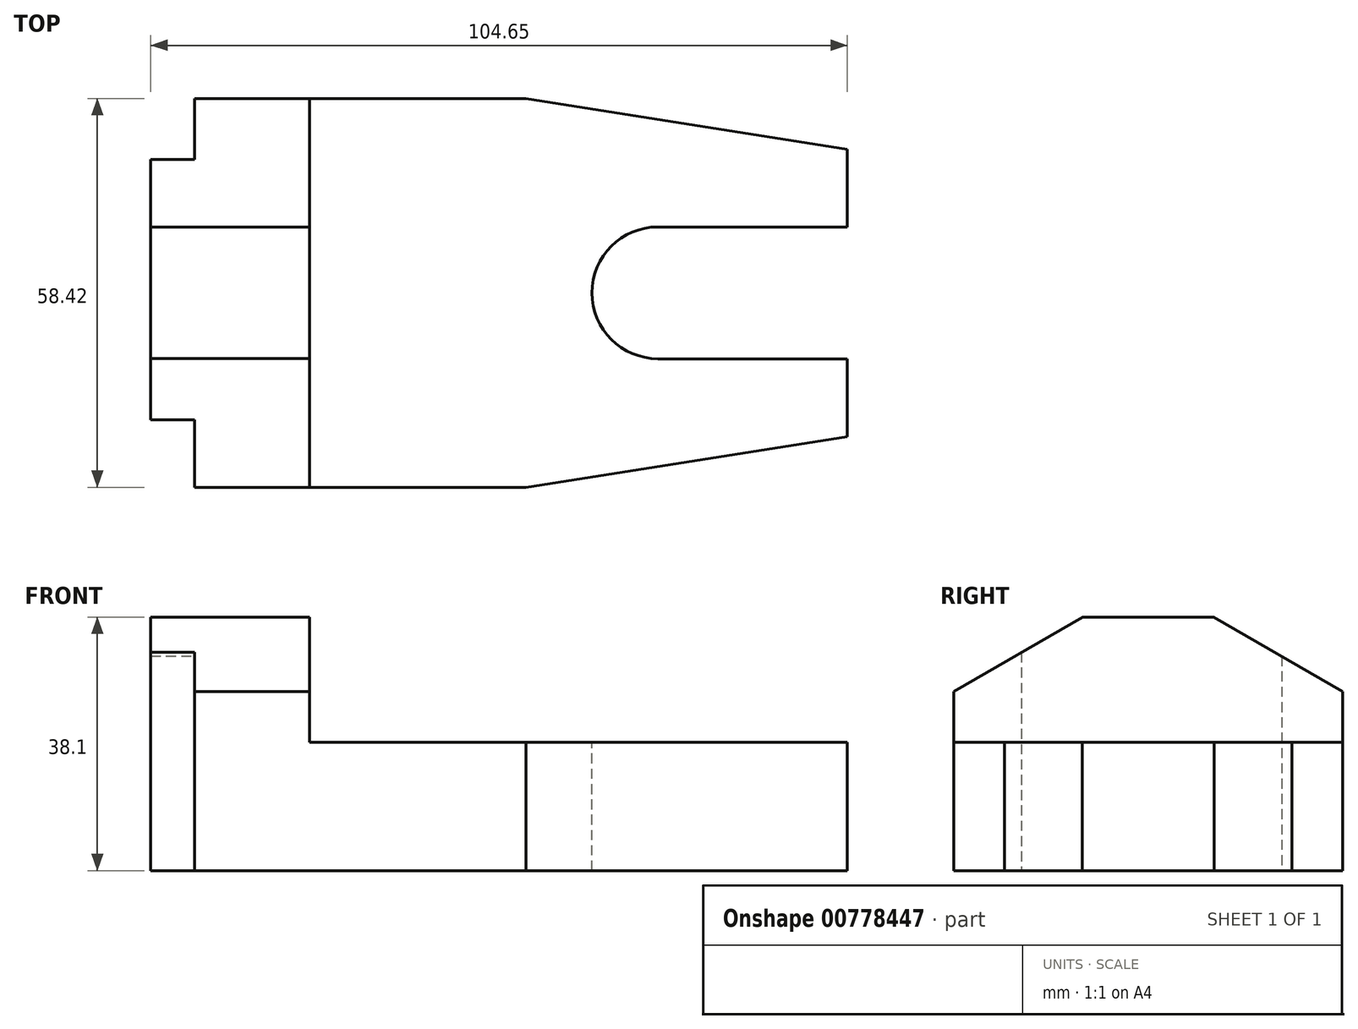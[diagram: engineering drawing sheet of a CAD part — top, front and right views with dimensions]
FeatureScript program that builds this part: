
annotation { "Feature Type Name" : "Feature", "Feature Type Description" : "" }
export const myFeature = defineFeature(function(context is Context, id is Id, definition is map)
    precondition{}
    {
        {
            var Q0;
            Q0=qCreatedBy(makeId("Front.planeOp"),FACE);
            var sketch = newSketch(context, id + "F0", { "sketchPlane" : qUnion([Q0])});
            skLineSegment(sketch, "E0.bottom", {"start": v(0, 0) * mm, "end": v(104.65, 0) * mm});
            skLineSegment(sketch, "E0.top", {"start": v(0, 38.1) * mm, "end": v(104.65, 38.1) * mm});
            skLineSegment(sketch, "E0.left", {"start": v(0, 0) * mm, "end": v(0, 38.1) * mm});
            skLineSegment(sketch, "E0.right", {"start": v(104.65, 0) * mm, "end": v(104.65, 38.1) * mm});
            skSolve(sketch);
        }
        {
            var Q0;
            Q0 = qSketchRegion(id + "F0", true);
            extrude(context, id + "F1", {"entities" : qUnion([Q0]), "depth" : 58.42 * mm, "offsetDistance" : 25.4 * mm});
        }
        {
            var Q0;
            Q0=makeQuery(id+"F1.opExtrude","CAP_FACE",FACE,{"disambiguationData":[OSD([sQuery(id+"F0.wireOp",EDGE,"E0.bottom"),sQuery(id+"F0.wireOp",EDGE,"E0.top"),sQuery(id+"F0.wireOp",EDGE,"E0.left"),sQuery(id+"F0.wireOp",EDGE,"E0.right")])],"isStart":false});
            var sketch = newSketch(context, id + "F2", { "sketchPlane" : qUnion([Q0])});
            skLineSegment(sketch, "E1", {"start": v(0, 38.1) * mm, "end": v(23.88, 38.1) * mm});
            skLineSegment(sketch, "E2", {"start": v(23.88, 38.1) * mm, "end": v(23.88, 19.3) * mm});
            skLineSegment(sketch, "E3", {"start": v(23.88, 19.3) * mm, "end": v(104.65, 19.3) * mm});
            skLineSegment(sketch, "E4", {"start": v(104.65, 19.3) * mm, "end": v(104.65, 0) * mm});
            skSolve(sketch);
        }
        {
            var Q0;
            {var subQ0=sQuery(id+"F2.wireOp",EDGE,"E2");Q0=makeQuery(id+"F2.imprint","IMPRINT",FACE,{"disambiguationData":[TD([[makeQuery(id+"F2.imprint","IMPRINT",EDGE,{"derivedFrom":subQ0}),1.0]])]});}
            extrude(context, id + "F3", {"entities" : qUnion([Q0]), "operationType" : NewBodyOperationType.REMOVE, "oppositeDirection" : true, "depth" : 58.42 * mm, "offsetDistance" : 25.4 * mm});
        }
        {
            var Q0;
            Q0=makeQuery(id+"F3.boolean.opBoolean","COPY",FACE,{"derivedFrom":makeQuery(id+"F3.opExtrude","SWEPT_FACE",FACE,{"disambiguationData":[OSD([sQuery(id+"F2.wireOp",EDGE,"E3")])]})});
            var sketch = newSketch(context, id + "F4", { "sketchPlane" : qUnion([Q0])});
            skLineSegment(sketch, "E5", {"start": v(104.65, -58.42) * mm, "end": v(56.39, -58.42) * mm});
            skLineSegment(sketch, "E6", {"start": v(56.39, -58.42) * mm, "end": v(104.65, -50.8) * mm});
            skLineSegment(sketch, "E7", {"start": v(104.65, -50.8) * mm, "end": v(104.65, -39.12) * mm});
            skLineSegment(sketch, "E8", {"start": v(104.65, -39.12) * mm, "end": v(104.65, -19.3) * mm});
            skLineSegment(sketch, "E9", {"start": v(104.65, -19.3) * mm, "end": v(104.65, -7.62) * mm});
            skLineSegment(sketch, "E10", {"start": v(104.65, -7.62) * mm, "end": v(56.39, 0) * mm});
            skLineSegment(sketch, "E11", {"start": v(56.39, 0) * mm, "end": v(104.65, 0) * mm});
            skLineSegment(sketch, "E12", {"start": v(104.65, 0) * mm, "end": v(104.65, -7.62) * mm});
            skLineSegment(sketch, "E13", {"start": v(104.65, -19.3) * mm, "end": v(76.2, -19.3) * mm});
            skLineSegment(sketch, "E14", {"start": v(104.65, -39.12) * mm, "end": v(76.2, -39.12) * mm});
            skLineSegment(sketch, "E15", {"start": v(76.2, -39.12) * mm, "end": v(76.2, -19.3) * mm});
            skLineSegment(sketch, "E16", {"start": v(76.2, -19.3) * mm, "end": v(76.2, -29.2) * mm});
            skArc(sketch, "E17", {"start": v(76.2, -19.3) * mm, "mid": v(66.3, -29.21) * mm, "end": v(76.2, -39.12) * mm});
            skSolve(sketch);
        }
        {
            var Q0;
            Q0=makeQuery(id+"F4.imprint","IMPRINT",FACE,{"disambiguationData":[TD([[makeQuery(id+"F4.imprint","IMPRINT",EDGE,{"derivedFrom":sQuery(id+"F4.wireOp",EDGE,"E10")}),-1.0]])]});
            var Q1;
            Q1=makeQuery(id+"F4.imprint","IMPRINT",FACE,{"disambiguationData":[TD([[makeQuery(id+"F4.imprint","IMPRINT",EDGE,{"derivedFrom":sQuery(id+"F4.wireOp",EDGE,"E8")}),-1.0]])]});
            var Q2;
            Q2=makeQuery(id+"F4.imprint","IMPRINT",FACE,{"disambiguationData":[TD([[makeQuery(id+"F4.imprint","IMPRINT",EDGE,{"derivedFrom":sQuery(id+"F4.wireOp",EDGE,"E15")}),1.0]])]});
            var Q3;
            {var subQ0=sQuery(id+"F4.wireOp",EDGE,"E5");Q3=makeQuery(id+"F4.imprint","IMPRINT",FACE,{"disambiguationData":[TD([[makeQuery(id+"F4.imprint","IMPRINT",EDGE,{"derivedFrom":subQ0}),1.0]])]});}
            extrude(context, id + "F5", {"entities" : qUnion([Q0, Q1, Q2, Q3]), "operationType" : NewBodyOperationType.REMOVE, "oppositeDirection" : true, "depth" : 19.3 * mm, "offsetDistance" : 25.4 * mm});
        }
        {
            var Q0;
            Q0=makeQuery(id+"F1.opExtrude","SWEPT_FACE",FACE,{"disambiguationData":[OSD([sQuery(id+"F0.wireOp",EDGE,"E0.left")])]});
            var sketch = newSketch(context, id + "F6", { "sketchPlane" : qUnion([Q0])});
            skLineSegment(sketch, "E18", {"start": v(58.42, 38.1) * mm, "end": v(48.26, 38.1) * mm});
            skLineSegment(sketch, "E19", {"start": v(48.26, 38.1) * mm, "end": v(48.26, 0) * mm});
            skLineSegment(sketch, "E20", {"start": v(0, 38.1) * mm, "end": v(10.16, 38.1) * mm});
            skLineSegment(sketch, "E21", {"start": v(9.17, 38.22) * mm, "end": v(9.17, 0) * mm});
            skSolve(sketch);
        }
        {
            var Q0;
            {var subQ1=sQuery(id+"F0.wireOp",EDGE,"E0.left");var subQ2=makeQuery(id+"F1.opExtrude","CAP_EDGE",EDGE,{"disambiguationData":[OSD([subQ1])],"isStart":true});Q0=makeQuery(id+"F6.imprint","IMPRINT",FACE,{"disambiguationData":[TD([[makeQuery(id+"F6.imprint","IMPRINT",EDGE,{"derivedFrom":subQ2}),-1.0]])]});}
            var Q1;
            Q1=makeQuery(id+"F6.imprint","IMPRINT",FACE,{"disambiguationData":[TD([[makeQuery(id+"F6.imprint","IMPRINT",EDGE,{"derivedFrom":sQuery(id+"F6.wireOp",EDGE,"E18")}),1.0]])]});
            extrude(context, id + "F7", {"entities" : qUnion([Q0, Q1]), "operationType" : NewBodyOperationType.REMOVE, "oppositeDirection" : true, "depth" : 6.6 * mm, "offsetDistance" : 25.4 * mm});
        }
        {
            var Q0;
            Q0=makeQuery(id+"F3.boolean.opBoolean","COPY",FACE,{"derivedFrom":makeQuery(id+"F3.opExtrude","SWEPT_FACE",FACE,{"disambiguationData":[OSD([sQuery(id+"F2.wireOp",EDGE,"E2")])]})});
            var sketch = newSketch(context, id + "F8", { "sketchPlane" : qUnion([Q0])});
            skLineSegment(sketch, "E22", {"start": v(0, 19.3) * mm, "end": v(0, 26.92) * mm});
            skLineSegment(sketch, "E23", {"start": v(0, 26.92) * mm, "end": v(-19.36, 38.1) * mm});
            skLineSegment(sketch, "E24", {"start": v(-19.36, 38.1) * mm, "end": v(0, 38.1) * mm});
            skLineSegment(sketch, "E25", {"start": v(0, 38.1) * mm, "end": v(0, 26.92) * mm});
            skSolve(sketch);
        }
        {
            var Q0;
            Q0=makeQuery(id+"F8.imprint","IMPRINT",FACE,{"disambiguationData":[TD([[makeQuery(id+"F8.imprint","IMPRINT",EDGE,{"derivedFrom":sQuery(id+"F8.wireOp",EDGE,"E23")}),-1.0]])]});
            extrude(context, id + "F9", {"entities" : qUnion([Q0]), "operationType" : NewBodyOperationType.REMOVE, "oppositeDirection" : true, "depth" : 23.88 * mm, "offsetDistance" : 25.4 * mm});
        }
        {
            var Q0;
            Q0=makeQuery(id+"F3.boolean.opBoolean","COPY",FACE,{"derivedFrom":makeQuery(id+"F3.opExtrude","SWEPT_FACE",FACE,{"disambiguationData":[OSD([sQuery(id+"F2.wireOp",EDGE,"E2")])]})});
            var sketch = newSketch(context, id + "F10", { "sketchPlane" : qUnion([Q0])});
            skLineSegment(sketch, "E26", {"start": v(-58.42, 19.3) * mm, "end": v(-58.42, 26.92) * mm});
            skLineSegment(sketch, "E27", {"start": v(-58.42, 26.92) * mm, "end": v(-39.06, 38.1) * mm});
            skLineSegment(sketch, "E28", {"start": v(-39.06, 38.1) * mm, "end": v(-58.42, 38.1) * mm});
            skLineSegment(sketch, "E29", {"start": v(-58.42, 38.1) * mm, "end": v(-58.42, 26.92) * mm});
            skSolve(sketch);
        }
        {
            var Q0;
            Q0 = qSketchRegion(id + "F10", true);
            extrude(context, id + "F11", {"entities" : qUnion([Q0]), "operationType" : NewBodyOperationType.REMOVE, "oppositeDirection" : true, "depth" : 23.88 * mm, "offsetDistance" : 25.4 * mm});
        }
    });
